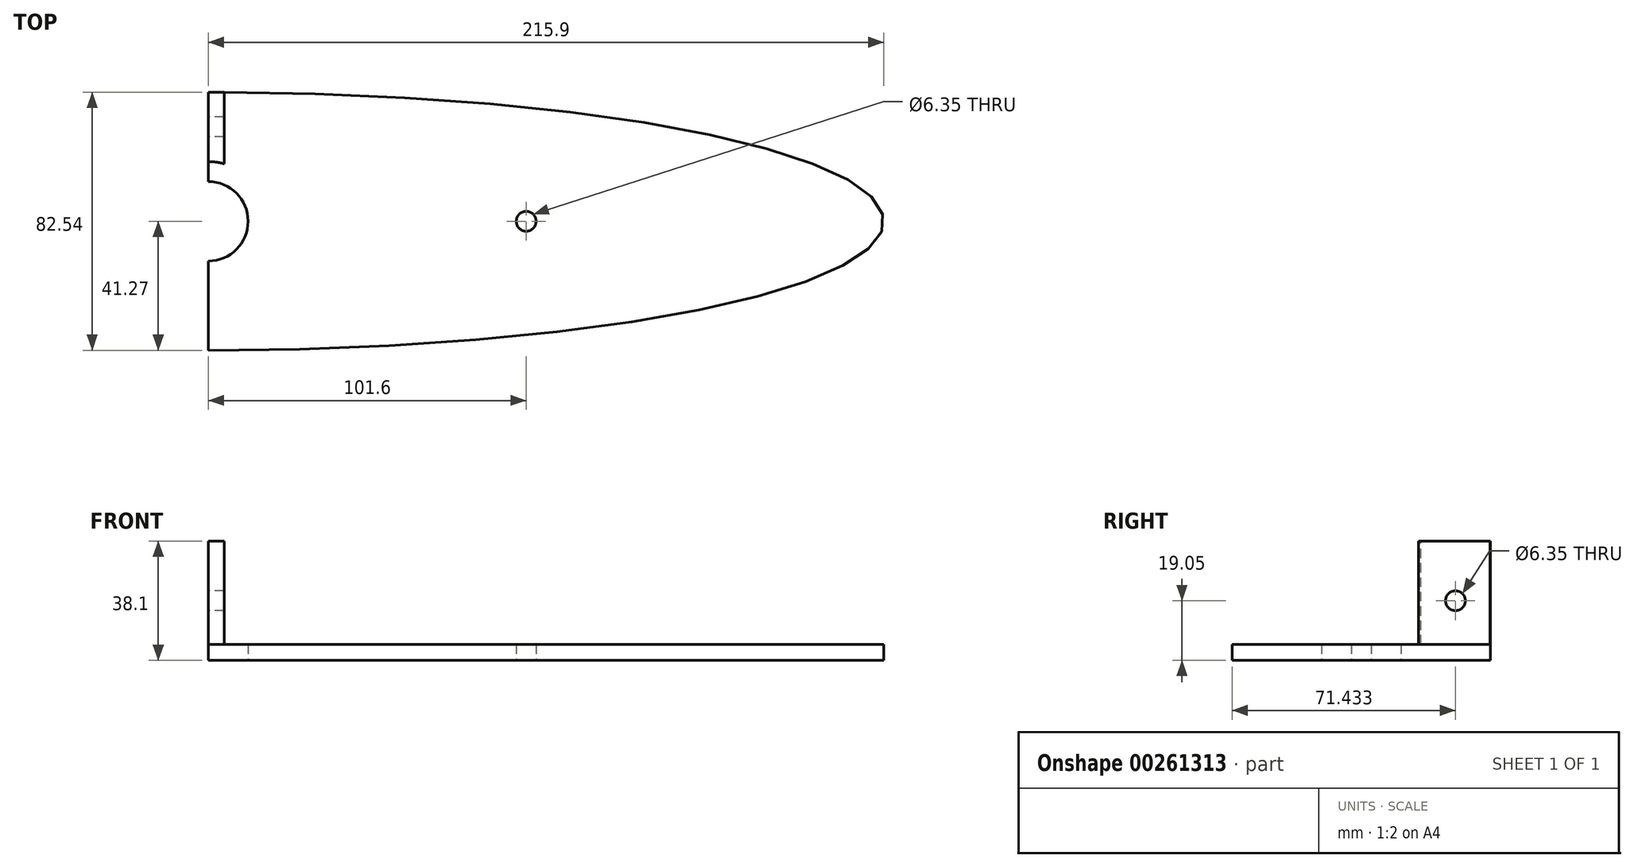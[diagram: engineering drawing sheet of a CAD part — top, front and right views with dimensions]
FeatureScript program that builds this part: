
annotation { "Feature Type Name" : "Feature", "Feature Type Description" : "" }
export const myFeature = defineFeature(function(context is Context, id is Id, definition is map)
    precondition{}
    {
        {
            var Q0;
            Q0=qCreatedBy(makeId("Top.planeOp"),FACE);
            var sketch = newSketch(context, id + "F0", { "sketchPlane" : qUnion([Q0])});
            skPoint(sketch, "E0", {"position": v(0, 41.28) * mm});
            skPoint(sketch, "E1", {"position": v(0, -41.28) * mm});
            skPoint(sketch, "E2", {"position": v(215.9, 0) * mm});
            skEllipticalArc(sketch, "E3", {});
            skLineSegment(sketch, "E4", {"start": v(0, 41.28) * mm, "end": v(0, 12.7) * mm});
            skArc(sketch, "E5", {"start": v(0, -12.7) * mm, "mid": v(12.7, 0) * mm, "end": v(0, 12.7) * mm});
            skLineSegment(sketch, "E6.trimOffspring", {"start": v(0, -12.7) * mm, "end": v(0, -41.28) * mm});
            skCircle(sketch, "E7", {"center": v(101.6, 0) * mm, "radius": 3.18 * mm});
            const initialGuessF0  = {"E3": [0, 0, 1, 0, 0.2159, 0.041275, 4.71238898038469, 1.5707963267948966]};
            skSetInitialGuess(sketch, initialGuessF0);
            skSolve(sketch);
        }
        {
            var Q0;
            Q0=makeQuery(id+"F0.imprint","IMPRINT",FACE,{"disambiguationData":[TD([[makeQuery(id+"F0.imprint","IMPRINT",EDGE,{"derivedFrom":sQuery(id+"F0.wireOp",EDGE,"E3")}),1.0]])]});
            extrude(context, id + "F1", {"entities" : qUnion([Q0]), "depth" : 38.1 * mm});
        }
        {
            var Q0;
            Q0=makeQuery(id+"F1.opExtrude","CAP_FACE",FACE,{"disambiguationData":[OSD([sQuery(id+"F0.wireOp",EDGE,"E3"),sQuery(id+"F0.wireOp",EDGE,"E4"),sQuery(id+"F0.wireOp",EDGE,"E5"),sQuery(id+"F0.wireOp",EDGE,"E6.trimOffspring"),sQuery(id+"F0.wireOp",EDGE,"E7")])],"isStart":false});
            var sketch = newSketch(context, id + "F2", { "sketchPlane" : qUnion([Q0])});
            skFitSpline(sketch, "E8.0", {"points": [v(210.73, -1.22) * mm, v(210.86, 0) * mm, v(210.73, 1.22) * mm, v(210.28, 2.59) * mm, v(209.41, 4.16) * mm, v(208.04, 5.9) * mm, v(206.13, 7.78) * mm, v(202.86, 10.38) * mm, v(197.42, 13.75) * mm, v(188.85, 17.75) * mm, v(180.1, 20.99) * mm, v(172.16, 23.47) * mm, v(165.76, 25.29) * mm, v(160.06, 26.75) * mm, v(155.28, 27.88) * mm, v(151.59, 28.72) * mm, v(147.8, 29.53) * mm, v(142.64, 30.6) * mm, v(135.98, 31.86) * mm, v(127.68, 33.28) * mm, v(116.22, 35.06) * mm, v(101.23, 37.04) * mm, v(82.3, 39) * mm, v(62.56, 40.57) * mm, v(45.57, 41.51) * mm, v(31.73, 42.04) * mm, v(21.24, 42.33) * mm, v(12.43, 42.48) * mm, v(5.34, 42.54) * mm, v(0, 42.55) * mm, v(-5.34, 42.54) * mm, v(-12.43, 42.48) * mm, v(-21.24, 42.33) * mm, v(-31.73, 42.04) * mm, v(-45.57, 41.51) * mm, v(-62.56, 40.57) * mm, v(-82.3, 39) * mm, v(-101.23, 37.04) * mm, v(-116.22, 35.06) * mm, v(-127.68, 33.28) * mm, v(-135.98, 31.86) * mm, v(-142.64, 30.6) * mm, v(-147.8, 29.53) * mm, v(-151.59, 28.72) * mm, v(-155.28, 27.88) * mm, v(-160.06, 26.75) * mm, v(-165.76, 25.29) * mm, v(-172.16, 23.47) * mm, v(-180.1, 20.99) * mm, v(-188.85, 17.75) * mm, v(-197.42, 13.75) * mm, v(-202.86, 10.38) * mm, v(-206.13, 7.78) * mm, v(-208.04, 5.9) * mm, v(-209.41, 4.16) * mm, v(-210.28, 2.59) * mm, v(-210.73, 1.22) * mm, v(-210.86, 0) * mm, v(-210.73, -1.22) * mm, v(-210.28, -2.59) * mm, v(-209.41, -4.16) * mm, v(-208.04, -5.9) * mm, v(-206.13, -7.78) * mm, v(-202.86, -10.38) * mm, v(-197.42, -13.75) * mm, v(-188.85, -17.75) * mm, v(-180.1, -20.99) * mm, v(-172.16, -23.47) * mm, v(-165.76, -25.29) * mm, v(-160.06, -26.75) * mm, v(-155.28, -27.88) * mm, v(-151.59, -28.72) * mm, v(-147.8, -29.53) * mm, v(-142.64, -30.6) * mm, v(-135.98, -31.86) * mm, v(-127.68, -33.28) * mm, v(-116.22, -35.06) * mm, v(-101.23, -37.04) * mm, v(-82.3, -39) * mm, v(-62.56, -40.57) * mm, v(-45.57, -41.51) * mm, v(-31.73, -42.04) * mm, v(-21.24, -42.33) * mm, v(-12.43, -42.48) * mm, v(-5.34, -42.54) * mm, v(0, -42.55) * mm, v(5.34, -42.54) * mm, v(12.43, -42.48) * mm, v(21.24, -42.33) * mm, v(31.73, -42.04) * mm, v(45.57, -41.51) * mm, v(62.56, -40.57) * mm, v(82.3, -39) * mm, v(101.23, -37.04) * mm, v(116.22, -35.06) * mm, v(127.68, -33.28) * mm, v(135.98, -31.86) * mm, v(142.64, -30.6) * mm, v(147.8, -29.53) * mm, v(151.59, -28.72) * mm, v(155.28, -27.88) * mm, v(160.06, -26.75) * mm, v(165.76, -25.29) * mm, v(172.16, -23.47) * mm, v(180.1, -20.99) * mm, v(188.85, -17.75) * mm, v(197.42, -13.75) * mm, v(202.86, -10.38) * mm, v(206.13, -7.78) * mm, v(208.04, -5.9) * mm, v(209.41, -4.16) * mm, v(210.28, -2.59) * mm, v(210.73, -1.22) * mm, v(210.86, 0) * mm, v(210.73, 1.22) * mm]});
            skLineSegment(sketch, "E9", {"start": v(0, -36.2) * mm, "end": v(0, -12.7) * mm});
            skLineSegment(sketch, "E10", {"start": v(0, -12.7) * mm, "end": v(0, 36.2) * mm});
            skLineSegment(sketch, "E11", {"start": v(5.08, 112.38) * mm, "end": v(5.08, 36.18) * mm});
            skLineSegment(sketch, "E12", {"start": v(5.83, -36.18) * mm, "end": v(5.83, -18.14) * mm});
            skLineSegment(sketch, "E13", {"start": v(5.08, 36.18) * mm, "end": v(5.08, 18.36) * mm});
            skArc(sketch, "E14", {"start": v(5.08, 18.36) * mm, "mid": v(-19.05, -0.39) * mm, "end": v(5.83, -18.14) * mm});
            skSolve(sketch);
        }
        {
            var Q0;
            Q0=makeQuery(id+"F2.imprint","IMPRINT",FACE,{"disambiguationData":[TD([[makeQuery(id+"F2.imprint","IMPRINT",EDGE,{"derivedFrom":makeQuery(id+"F1.opExtrude","CAP_EDGE",EDGE,{"disambiguationData":[OSD([sQuery(id+"F0.wireOp",EDGE,"E7")])],"isStart":false})}),-1.0]])]});
            extrude(context, id + "F3", {"entities" : qUnion([Q0]), "operationType" : NewBodyOperationType.REMOVE, "oppositeDirection" : true, "depth" : 33.02 * mm});
        }
        {
            var Q0;
            Q0=makeQuery(id+"F1.opExtrude","SWEPT_FACE",FACE,{"disambiguationData":[OSD([sQuery(id+"F0.wireOp",EDGE,"E6.trimOffspring")])]});
            var sketch = newSketch(context, id + "F4", { "sketchPlane" : qUnion([Q0])});
            skCircle(sketch, "E15", {"center": v(-30.16, 19.05) * mm, "radius": 3.18 * mm});
            skPoint(sketch, "E16", {"position": v(-41.28, 19.05) * mm});
            skPoint(sketch, "E17", {"position": v(-30.16, 38.1) * mm});
            skCircle(sketch, "E18.MirrorC", {"center": v(30.16, 19.05) * mm, "radius": 3.18 * mm});
            skSolve(sketch);
        }
        {
            var Q0;
            Q0=makeQuery(id+"F4.imprint","IMPRINT",FACE,{"disambiguationData":[TD([[makeQuery(id+"F4.imprint","IMPRINT",EDGE,{"derivedFrom":sQuery(id+"F4.wireOp",EDGE,"E15")}),1.0]])]});
            var Q1;
            Q1=makeQuery(id+"F4.imprint","IMPRINT",FACE,{"disambiguationData":[TD([[makeQuery(id+"F4.imprint","IMPRINT",EDGE,{"derivedFrom":sQuery(id+"F4.wireOp",EDGE,"E18.MirrorC")}),-1.0]])]});
            extrude(context, id + "F5", {"entities" : qUnion([Q0, Q1]), "operationType" : NewBodyOperationType.REMOVE, "oppositeDirection" : true, "depth" : 25.4 * mm});
        }
    });
